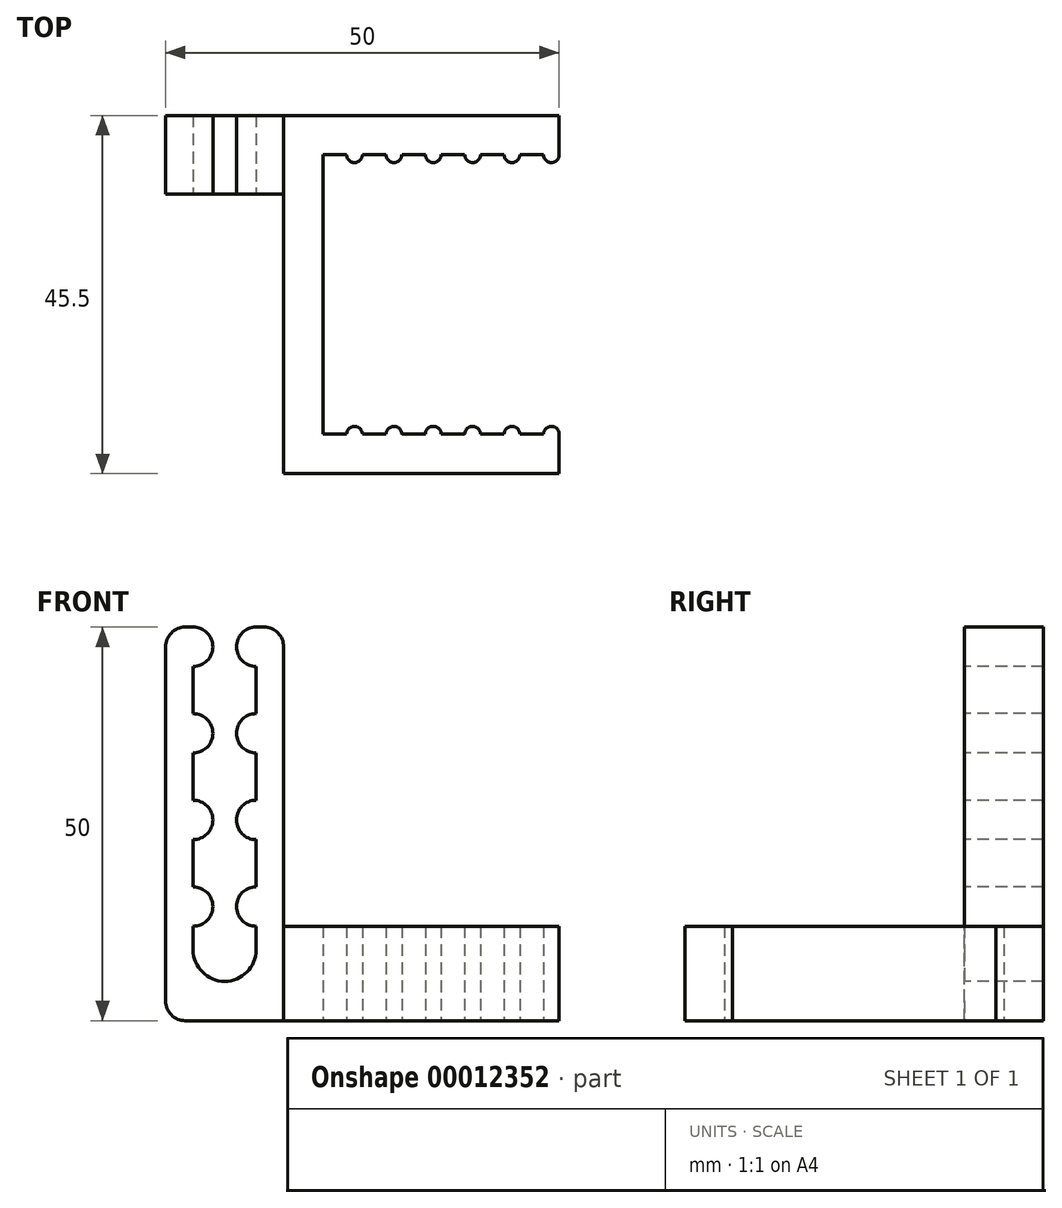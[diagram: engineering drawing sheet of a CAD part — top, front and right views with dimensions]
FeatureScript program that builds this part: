
annotation { "Feature Type Name" : "Feature", "Feature Type Description" : "" }
export const myFeature = defineFeature(function(context is Context, id is Id, definition is map)
    precondition{}
    {
        {
            var Q0;
            Q0=qCreatedBy(makeId("Top.planeOp"),FACE);
            var sketch = newSketch(context, id + "F0", { "sketchPlane" : qUnion([Q0])});
            skLineSegment(sketch, "E0", {"start": v(0, 0) * mm, "end": v(3, 0) * mm});
            skLineSegment(sketch, "E1", {"start": v(30, 0) * mm, "end": v(30, -5) * mm});
            skLineSegment(sketch, "E2", {"start": v(30, -5) * mm, "end": v(-5, -5) * mm});
            skLineSegment(sketch, "E3", {"start": v(-5, -5) * mm, "end": v(-5, 40.5) * mm});
            skLineSegment(sketch, "E4", {"start": v(-5, 40.5) * mm, "end": v(30, 40.5) * mm});
            skLineSegment(sketch, "E5", {"start": v(30, 40.5) * mm, "end": v(30, 35.5) * mm});
            skLineSegment(sketch, "E6", {"start": v(0, 35.5) * mm, "end": v(0, 0) * mm});
            skLineSegment(sketch, "E7", {"start": v(0, 17.75) * mm, "end": v(34.89, 17.75) * mm, "construction": true});
            skArc(sketch, "E8", {"start": v(3, 35.5) * mm, "mid": v(4, 34.5) * mm, "end": v(5, 35.5) * mm});
            skArc(sketch, "E9.1.0.0", {"start": v(8, 35.5) * mm, "mid": v(9, 34.5) * mm, "end": v(10, 35.5) * mm});
            skArc(sketch, "E9.2.0.0", {"start": v(13, 35.5) * mm, "mid": v(14, 34.5) * mm, "end": v(15, 35.5) * mm});
            skArc(sketch, "E9.3.0.0", {"start": v(18, 35.5) * mm, "mid": v(19, 34.5) * mm, "end": v(20, 35.5) * mm});
            skArc(sketch, "E9.4.0.0", {"start": v(23, 35.5) * mm, "mid": v(24, 34.5) * mm, "end": v(25, 35.5) * mm});
            skArc(sketch, "E9.5.0.0", {"start": v(28, 35.5) * mm, "mid": v(29, 34.5) * mm, "end": v(30, 35.5) * mm});
            skLineSegment(sketch, "E9.direction1", {"start": v(4, 35.5) * mm, "end": v(9, 35.5) * mm, "construction": true});
            skArc(sketch, "E10.0.MirrorC", {"start": v(28, 0) * mm, "mid": v(29, 1) * mm, "end": v(30, 0) * mm});
            skArc(sketch, "E11.0.MirrorC", {"start": v(23, 0) * mm, "mid": v(24, 1) * mm, "end": v(25, 0) * mm});
            skArc(sketch, "E12.0.MirrorC", {"start": v(18, 0) * mm, "mid": v(19, 1) * mm, "end": v(20, 0) * mm});
            skArc(sketch, "E13.0.MirrorC", {"start": v(13, 0) * mm, "mid": v(14, 1) * mm, "end": v(15, 0) * mm});
            skArc(sketch, "E14.0.MirrorC", {"start": v(8, 0) * mm, "mid": v(9, 1) * mm, "end": v(10, 0) * mm});
            skArc(sketch, "E15.0.MirrorC", {"start": v(3, 0) * mm, "mid": v(4, 1) * mm, "end": v(5, 0) * mm});
            skLineSegment(sketch, "E16.trimOffspring", {"start": v(3, 35.5) * mm, "end": v(0, 35.5) * mm});
            skLineSegment(sketch, "E17.trimOffspring", {"start": v(8, 35.5) * mm, "end": v(5, 35.5) * mm});
            skLineSegment(sketch, "E18.trimOffspring", {"start": v(13, 35.5) * mm, "end": v(10, 35.5) * mm});
            skLineSegment(sketch, "E19.trimOffspring", {"start": v(18, 35.5) * mm, "end": v(15, 35.5) * mm});
            skLineSegment(sketch, "E20.trimOffspring", {"start": v(23, 35.5) * mm, "end": v(20, 35.5) * mm});
            skLineSegment(sketch, "E21.trimOffspring", {"start": v(28, 35.5) * mm, "end": v(25, 35.5) * mm});
            skLineSegment(sketch, "E22.trimOffspring", {"start": v(5, 0) * mm, "end": v(8, 0) * mm});
            skLineSegment(sketch, "E23.trimOffspring", {"start": v(10, 0) * mm, "end": v(13, 0) * mm});
            skLineSegment(sketch, "E24.trimOffspring", {"start": v(15, 0) * mm, "end": v(18, 0) * mm});
            skLineSegment(sketch, "E25.trimOffspring", {"start": v(20, 0) * mm, "end": v(23, 0) * mm});
            skLineSegment(sketch, "E26.trimOffspring", {"start": v(25, 0) * mm, "end": v(28, 0) * mm});
            skSolve(sketch);
        }
        {
            var Q0;
            Q0=makeQuery(id+"F0.imprint","IMPRINT",FACE,{"disambiguationData":[TD([[makeQuery(id+"F0.imprint","IMPRINT",EDGE,{"derivedFrom":sQuery(id+"F0.wireOp",EDGE,"E0")}),-1.0]])]});
            extrude(context, id + "F1", {"entities" : qUnion([Q0]), "depth" : 12 * mm});
        }
        {
            var Q0;
            Q0=makeQuery(id+"F1.opExtrude","SWEPT_FACE",FACE,{"disambiguationData":[OSD([sQuery(id+"F0.wireOp",EDGE,"E3")])]});
            var sketch = newSketch(context, id + "F2", { "sketchPlane" : qUnion([Q0])});
            skLineSegment(sketch, "E27.bottom", {"start": v(-40.5, 0) * mm, "end": v(-30.5, 0) * mm});
            skLineSegment(sketch, "E27.top", {"start": v(-40.5, 50) * mm, "end": v(-30.5, 50) * mm});
            skLineSegment(sketch, "E27.left", {"start": v(-40.5, 0) * mm, "end": v(-40.5, 50) * mm});
            skLineSegment(sketch, "E27.right", {"start": v(-30.5, 0) * mm, "end": v(-30.5, 50) * mm});
            skSolve(sketch);
        }
        {
            var Q0;
            {var subQ6=sQuery(id+"F2.wireOp",EDGE,"E27.bottom");Q0=makeQuery(id+"F2.imprint","IMPRINT",FACE,{"disambiguationData":[TD([[makeQuery(id+"F2.imprint","IMPRINT",EDGE,{"derivedFrom":subQ6}),-1.0]])]});}
            var Q1;
            {var subQ5=sQuery(id+"F2.wireOp",EDGE,"E27.top");Q1=makeQuery(id+"F2.imprint","IMPRINT",FACE,{"disambiguationData":[TD([[makeQuery(id+"F2.imprint","IMPRINT",EDGE,{"derivedFrom":subQ5}),-1.0]])]});}
            extrude(context, id + "F3", {"entities" : qUnion([Q0, Q1]), "operationType" : NewBodyOperationType.ADD, "depth" : 15 * mm});
        }
        {
            var Q0;
            Q0=makeQuery(id+"F3.opExtrude","SWEPT_FACE",FACE,{"disambiguationData":[OSD([sQuery(id+"F2.wireOp",EDGE,"E27.right")])]});
            var sketch = newSketch(context, id + "F4", { "sketchPlane" : qUnion([Q0])});
            skLineSegment(sketch, "E28.bottom", {"start": v(-17.5, 50) * mm, "end": v(-16.5, 50) * mm});
            skLineSegment(sketch, "E28.top", {"start": v(-17.5, 0) * mm, "end": v(-5, 0) * mm});
            skLineSegment(sketch, "E28.left", {"start": v(-20, 47.5) * mm, "end": v(-20, 2.5) * mm});
            skLineSegment(sketch, "E28.right", {"start": v(-5, 47.5) * mm, "end": v(-5, 0) * mm});
            skLineSegment(sketch, "E29", {"start": v(-8.5, 45) * mm, "end": v(-8.5, 39) * mm});
            skArc(sketch, "E30", {"start": v(-8.5, 9) * mm, "mid": v(-12.5, 5) * mm, "end": v(-16.5, 9) * mm});
            skLineSegment(sketch, "E31", {"start": v(-12.5, 9) * mm, "end": v(-12.5, 31.86) * mm, "construction": true});
            skLineSegment(sketch, "E32.trimOffspring", {"start": v(-8.5, 50) * mm, "end": v(-7.5, 50) * mm});
            skPoint(sketch, "E33.visualSharp", {"position": v(-20, 50) * mm});
            skArc(sketch, "E33.filletArc", {"start": v(-17.5, 50) * mm, "mid": v(-19.27, 49.27) * mm, "end": v(-20, 47.5) * mm});
            skPoint(sketch, "E34.visualSharp", {"position": v(-5, 50) * mm});
            skArc(sketch, "E34.filletArc", {"start": v(-5, 47.5) * mm, "mid": v(-5.73, 49.27) * mm, "end": v(-7.5, 50) * mm});
            skPoint(sketch, "E35.visualSharp", {"position": v(-20, 0) * mm});
            skArc(sketch, "E35.filletArc", {"start": v(-20, 2.5) * mm, "mid": v(-19.27, 0.73) * mm, "end": v(-17.5, 0) * mm});
            skArc(sketch, "E36", {"start": v(-16.5, 45) * mm, "mid": v(-14, 47.5) * mm, "end": v(-16.5, 50) * mm});
            skArc(sketch, "E37.1.0.0", {"start": v(-16.5, 34) * mm, "mid": v(-14, 36.5) * mm, "end": v(-16.5, 39) * mm});
            skArc(sketch, "E37.2.0.0", {"start": v(-16.5, 23) * mm, "mid": v(-14, 25.5) * mm, "end": v(-16.5, 28) * mm});
            skArc(sketch, "E37.3.0.0", {"start": v(-16.5, 12) * mm, "mid": v(-14, 14.5) * mm, "end": v(-16.5, 17) * mm});
            skLineSegment(sketch, "E37.direction1", {"start": v(-16.5, 47.5) * mm, "end": v(-16.5, 36.5) * mm, "construction": true});
            skArc(sketch, "E38.0.MirrorC", {"start": v(-8.5, 45) * mm, "mid": v(-11, 47.5) * mm, "end": v(-8.5, 50) * mm});
            skArc(sketch, "E39.0.MirrorC", {"start": v(-8.5, 34) * mm, "mid": v(-11, 36.5) * mm, "end": v(-8.5, 39) * mm});
            skArc(sketch, "E40.0.MirrorC", {"start": v(-8.5, 23) * mm, "mid": v(-11, 25.5) * mm, "end": v(-8.5, 28) * mm});
            skArc(sketch, "E41.0.MirrorC", {"start": v(-8.5, 12) * mm, "mid": v(-11, 14.5) * mm, "end": v(-8.5, 17) * mm});
            skLineSegment(sketch, "E42.trimOffspring", {"start": v(-16.5, 45) * mm, "end": v(-16.5, 39) * mm});
            skLineSegment(sketch, "E43.trimOffspring", {"start": v(-16.5, 34) * mm, "end": v(-16.5, 28) * mm});
            skLineSegment(sketch, "E44.trimOffspring", {"start": v(-8.5, 34) * mm, "end": v(-8.5, 28) * mm});
            skLineSegment(sketch, "E45.trimOffspring", {"start": v(-8.5, 23) * mm, "end": v(-8.5, 17) * mm});
            skLineSegment(sketch, "E46.trimOffspring", {"start": v(-8.5, 12) * mm, "end": v(-8.5, 9) * mm});
            skLineSegment(sketch, "E47.trimOffspring", {"start": v(-16.5, 12) * mm, "end": v(-16.5, 9) * mm});
            skLineSegment(sketch, "E48.trimOffspring", {"start": v(-16.5, 23) * mm, "end": v(-16.5, 17) * mm});
            skLineSegment(sketch, "E49.0", {"start": v(30, 12) * mm, "end": v(-5, 12) * mm});
            skLineSegment(sketch, "E50.top", {"start": v(30, 0) * mm, "end": v(-5, 0) * mm});
            skLineSegment(sketch, "E50.left", {"start": v(30, 12) * mm, "end": v(30, 0) * mm});
            skLineSegment(sketch, "E50.right", {"start": v(-5, 12) * mm, "end": v(-5, 0) * mm});
            skSolve(sketch);
        }
        {
            var Q0;
            Q0=makeQuery(id+"F4.imprint","IMPRINT",FACE,{"disambiguationData":[TD([[makeQuery(id+"F4.imprint","IMPRINT",EDGE,{"derivedFrom":sQuery(id+"F4.wireOp",EDGE,"E28.bottom")}),-1.0]])]});
            var Q1;
            Q1=makeQuery(id+"F1.opExtrude","SWEPT_FACE",FACE,{"disambiguationData":[OSD([sQuery(id+"F0.wireOp",EDGE,"E2")])]});
            extrude(context, id + "F5", {"entities" : qUnion([Q0, Q1]), "operationType" : NewBodyOperationType.INTERSECT, "endBound" : BoundingType.THROUGH_ALL, "oppositeDirection" : true, "depth" : 25 * mm});
        }
    });
